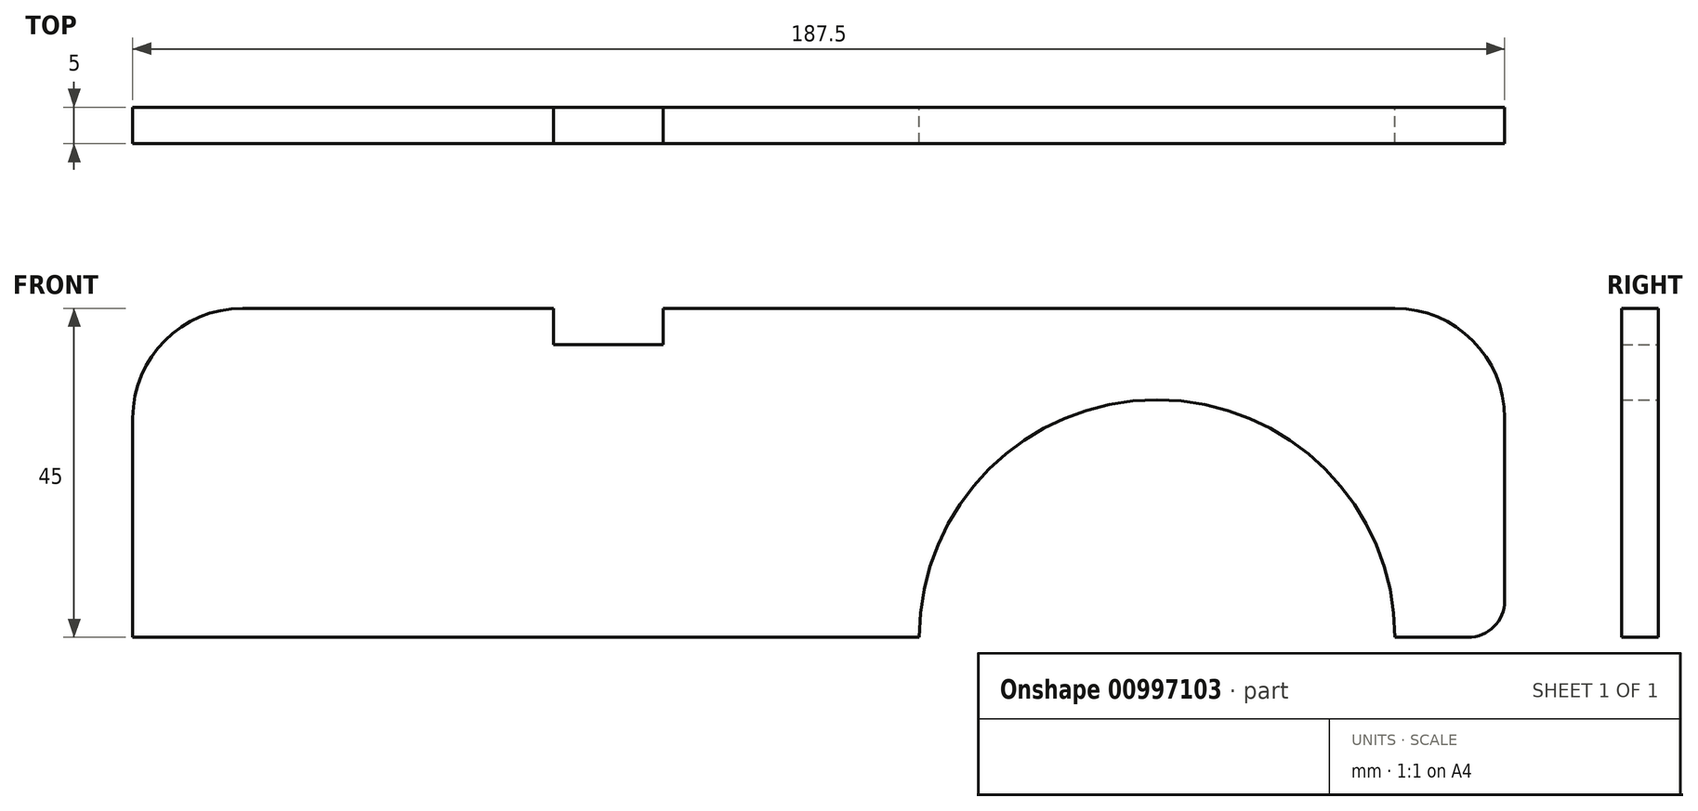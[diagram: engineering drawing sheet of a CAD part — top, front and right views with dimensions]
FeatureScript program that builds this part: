
annotation { "Feature Type Name" : "Feature", "Feature Type Description" : "" }
export const myFeature = defineFeature(function(context is Context, id is Id, definition is map)
    precondition{}
    {
        {
            var Q0;
            Q0=qCreatedBy(makeId("Front.planeOp"),FACE);
            var sketch = newSketch(context, id + "F0", { "sketchPlane" : qUnion([Q0])});
            skArc(sketch, "E0", {"start": v(32.5, 0) * mm, "mid": v(0, 32.5) * mm, "end": v(-32.5, 0) * mm});
            skLineSegment(sketch, "E1", {"start": v(-32.5, 0) * mm, "end": v(-130, 0) * mm});
            skLineSegment(sketch, "E2", {"start": v(-125, 45) * mm, "end": v(-82.5, 45) * mm});
            skLineSegment(sketch, "E3", {"start": v(47.5, 30) * mm, "end": v(47.5, 5) * mm});
            skLineSegment(sketch, "E4", {"start": v(42.5, 0) * mm, "end": v(32.5, 0) * mm});
            skPoint(sketch, "E5.visualSharp", {"position": v(47.5, 45) * mm});
            skArc(sketch, "E5.filletArc", {"start": v(47.5, 30) * mm, "mid": v(43.1, 40.6) * mm, "end": v(32.5, 45) * mm});
            skLineSegment(sketch, "E6", {"start": v(-82.5, 45) * mm, "end": v(-82.5, 40) * mm});
            skLineSegment(sketch, "E7", {"start": v(-82.5, 40) * mm, "end": v(-67.5, 40) * mm});
            skLineSegment(sketch, "E8", {"start": v(-67.5, 40) * mm, "end": v(-67.5, 45) * mm});
            skLineSegment(sketch, "E9.trimOffspring", {"start": v(-67.5, 45) * mm, "end": v(32.5, 45) * mm});
            skPoint(sketch, "E10", {"position": v(-75, 40) * mm});
            skPoint(sketch, "E11.visualSharp", {"position": v(47.5, 0) * mm});
            skArc(sketch, "E11.filletArc", {"start": v(42.5, 0) * mm, "mid": v(46.04, 1.46) * mm, "end": v(47.5, 5) * mm});
            skLineSegment(sketch, "E12", {"start": v(-125, 45) * mm, "end": v(-125, 45) * mm});
            skLineSegment(sketch, "E13", {"start": v(-140, 30) * mm, "end": v(-140, 0) * mm});
            skLineSegment(sketch, "E14", {"start": v(-140, 0) * mm, "end": v(-130, 0) * mm});
            skPoint(sketch, "E15.visualSharp", {"position": v(-140, 45) * mm});
            skArc(sketch, "E15.filletArc", {"start": v(-125, 45) * mm, "mid": v(-135.6, 40.6) * mm, "end": v(-140, 30) * mm});
            skSolve(sketch);
        }
        {
            var Q0;
            Q0=qSketchRegion(id+"F0",true);
            extrude(context, id + "F1", {"entities" : qUnion([Q0]), "depth" : 5 * mm, "offsetDistance" : 25 * mm});
        }
    });
